# Revit family: Building-ContenitoriIncasso-GEWISS-24SC-GREENWALL-SCATOLE-INCASSO_4P+4P
name_source: partatom
category: Apparecchi elettrici
revit_build: Autodesk Revit 2016 (Build: 20161004_0715(x64)
units: mm (PartAtom-declared; Revit-internal decimal feet)

## family parameters
Condiviso = Sì
Host = Superficie
Mantenere orientamento annotazione = Sì
Numero OmniClass = 23.80.30.14.24
Punto di calcolo locali = Sì
Quota connettore circolare = Usa diametro
Taglio con vuoti quando caricato = Sì
Tipo di parte = Normale
Titolo OmniClass = Junction Boxes

## types (1)
- GW24237PM - Halogen free - 8P (4+4)
    Caratteristiche = Halogen free
    Catalogo = BUILDING
    Catalogo Serie = 24SC
    Codice EAN = 8011564801868
    Codice Electrocod = 0110
    Descrizione = SCATOLA 8P.(4+4) PM ALTA CAPIENZA GREEN
    Descrizione prodotto = Per pannelli di comando
    Descrizione: = 8 posti (4+4)
    Dim. esterne BxHxP (mm) = 131x129x53
    Glow Wire Test = 850°C
    Grado di protezione = IP40
    IDF = 399a1d58-41fd-4a69-82fd-6fd820024719
    IDT = 39fe7c71-9ec4-408e-b869-c61f51db61d8
    Immagine tipo = GW24237PM.jpg
    Installazione = Incasso
    Interasse fissaggio supporti = 108,5MM
    Modello = GW24237PM
    N. moduli SYSTEM = 8 posti (4+4)
    Per Pareti = Cartongesso
    Predisposizione scomparti = 2
    Produttore = GEWISS S.p.A.
    Prospetto di default = 1219.2 mm  [stored 4 ft]
    Resistenza agli urti = IK07
    SEO = Scatola
    Scatola = GEWISS - scatola a incasso
    Scheda Tecnica = https://www.gewiss.com
    Temperatura di impiego = -15 +60 °C
    Termopressione con biglia = 70 °C
    Tipo Materiale = Halogen free secondo norma EN 50267-2-2
    Tipo: = Alta capienza
    URL = https://www.gewiss.com
    Versione file RFA = 19.0

note: [stored X ft] marks values corroborated as IEEE doubles in the binary element streams (Revit-internal decimal feet)

## geometry (parser evidence)
native form markers: Sweep x2
no freeform markers — native parametric forms only
